# Revit family: Sanitary_Taps-Mixers_AXOR_36110CHN-AXOR-Citterio-E-Single-lever-ba_new
name_source: partatom
category: Plumbing Fixtures
revit_build: Autodesk Revit 2018 (Build: 20170223_1515(x64)
units: mm (PartAtom-declared; Revit-internal decimal feet)

## family parameters
Always vertical = No
Cut with Voids When Loaded = No
OmniClass Number = 23.31.11.00
OmniClass Title = Faucets
Part Type = Normal
Room Calculation Point = No
Round Connector Dimension = Use Diameter
Shared = No
Work Plane-Based = Yes

## types (4) — shared parameters
Always visible = Yes
BIMobject category = Taps & Mixers
Connector Description = Water Inlet 12.7mm
Default Elevation = 1219.2 mm
Description = AXOR Citterio E Single lever basin mixer 130 with lever handle and pop-up waste set
Design country = Germany
Diameter = 12.7 mm  [stored 0.0416667 ft]
EAN code = 4059625378267
Edition number = 1
IFC Classification = Valve
Manufacturer = AXOR
Manufacturer country = Germany
Manufacturer name = AXOR
Model = 36110CHN
OmniClass Code = 23-31 11 00
OmniClass Description = Faucets
Product Guid = 7e60486a-23b7-4cb1-8880-2234a8573503
Product SKU = 36110CHN
Product data url = https://bimobject.com
Product family = AXOR Citterio E
Product group = Basin mixers
Product name = 36110CHN AXOR Citterio E Single lever basin mixer 130 with lever handle and pop-up waste set
QR code = https://bimobject.com
URL = https://www.axor-design.com
Weight Net (Kg) = 2.2

## per-type parameters (varying)
| type | Material 1 |
| 007 Chrome | AXOR - Metal - 007 Chrome |
| 677 Matt Black | AXOR - Metal - 677 Matt Black |
| 347 Brushed Black Chrome | AXOR - Metal - 347 Brushed Black Chrome |
| 997 Polished Gold Optic | AXOR - Metal - 997 Polished Gold Optic |

note: [stored X ft] marks values corroborated as IEEE doubles in the binary element streams (Revit-internal decimal feet)

## geometry (parser evidence)
native form markers: Sweep x1
no freeform markers — native parametric forms only
